# Revit family: Nuaire_IfcAirTerminal_Hts4_9_12
name_source: partatom
category: Air Terminals
revit_build: Autodesk Revit 2018 (Build: 20170223_1515(x64)
units: mm (PartAtom-declared; Revit-internal decimal feet)

## family parameters
Always vertical = Yes
Cut with Voids When Loaded = No
OmniClass Number = 23.75.00.00
OmniClass Title = Climate Control (HVAC)
Part Type = Normal
Room Calculation Point = No
Round Connector Dimension = Use Diameter
Shared = No
Work Plane-Based = No

## types (3) — shared parameters
6 Monthly = SFG20 26-01
Annually = SFG20 26-01
BMS Links = No
Battery Supply = No
CE Approval = Yes
COBie.Type = Yes
COBie.Type.Category = Air ventilation grilles
COBie.Type.DurationUnit = Years
COBie.Type.Manufacturer = Nuaire
COBie.Type.ModelNumber = HTS12
COBie.Type.ModelReference = HTS12
COBie.Type.Name = HTS12
COBie.Type.NominalHeight = 300 mm
COBie.Type.NominalLength = 609 mm
COBie.Type.NominalWidth = 609 mm
COBie.Type.WarrantyDescription = 5 years. First year parts and labour, further 4 years parts only.
COBie.Type.WarrantyDurationLabor = 1
COBie.Type.WarrantyDurationParts = 5
COBie.Type.WarrantyDurationUnit = Year
COBie.Type.WarrantyGuarantorLabor = Nuaire
COBie.Type.WarrantyGuarantorParts = Nuaire
Catalogue Pages = tba
Classification.Uniclass.Pr.Description = Air ventilation grilles
Classification.Uniclass.Pr.Number = Pr_30_59_94_04
Daily = SFG20 26-01
Enclosure Rating = Not Rated
Environmental Product Declaration = WEEE, RoHS
Fax Number = +44(0)2920-858-222
Fire Control Panel Links = No
Height = 300 mm
I&M Manual = http://nuaire.info
IFCExportAs = IfcAirTerminal
IFCExportType = GRILLE
Length = 609 mm
Location of Manufacturer = 51.571856, -3.232638
Maintenance Required 0 to 300hrs = http://nuaire.info
Maintenance Required 1001 to 2000hrs = http://nuaire.info
Maintenance Required 2001 to 4000hrs = http://nuaire.info
Maintenance Required 301 to 600hrs = http://nuaire.info
Maintenance Required 4001 to 8000hrs = http://nuaire.info
Maintenance Required 601 to 1000hrs = http://nuaire.info
Maintenance Required 8001 to 12000hrs = http://nuaire.info
Manufacturer = Nuaire
Manufacturer Website = http://www.nuaire.co.uk
Max Flow = 0.030 m³/s
Maximum Ambient Temperature = 40 °C
Model = HTS12
Monthly = SFG20 26-01
OmniClass Number = 23-33 49 23
OmniClass Title = Grilles
Operation and Maintenance Manual = http://nuaire.info
Postcode = CF83 1NA
Product Literature = http://nuaire.info
Product Range = Haven
Quarterly = SFG20 26-01
Reference Standard = ISO 9001:2015
Responsible Sourcing of Materials = FSC
Spigot Height = 90 mm  [stored 0.295276 ft]
Spigot Width = 220 mm
Telephone Number = +44(0)2920-858-200
URL = http://www.nuaire.co.uk
VAT Registration Number = 877308
Weatherproof or Internal Only = Internal
Weekly = SFG20 26-01
Weight = 15.00 kg
Width = 609 mm
zero-valued in all types: COBie.Type.Area, COBie.Type.ReplacementCost, Cost, Life Cycle Analysis

## per-type parameters (varying)
| type | COBie.Type.Description | Description | Revit Family Last Revised | hole_count |
| HTS12 | Haven Ceiling Mounted Supply Terminal with 12 Rotating Vents | Haven Ceiling Mounted Supply Terminal with 12 Rotating Vents | 2021-02-19T15:30:00 | 12 |
| HTS9 | Haven Ceiling Mounted Supply Terminal with 9 Rotating Vents | Haven Ceiling Mounted Supply Terminal with 9 Rotating Vents | 2021-02-19T15:30:00 | 9 |
| HTS4 | Haven Ceiling Mounted Supply Terminal with 4 Rotating Vents | Haven Ceiling Mounted Supply Terminal with 4 Rotating Vents | 2021-09-28T10:10:00 | 4 |

note: [stored X ft] marks values corroborated as IEEE doubles in the binary element streams (Revit-internal decimal feet)

## geometry (parser evidence)
native form markers: Blend x28, Sweep x14
no freeform markers — native parametric forms only
